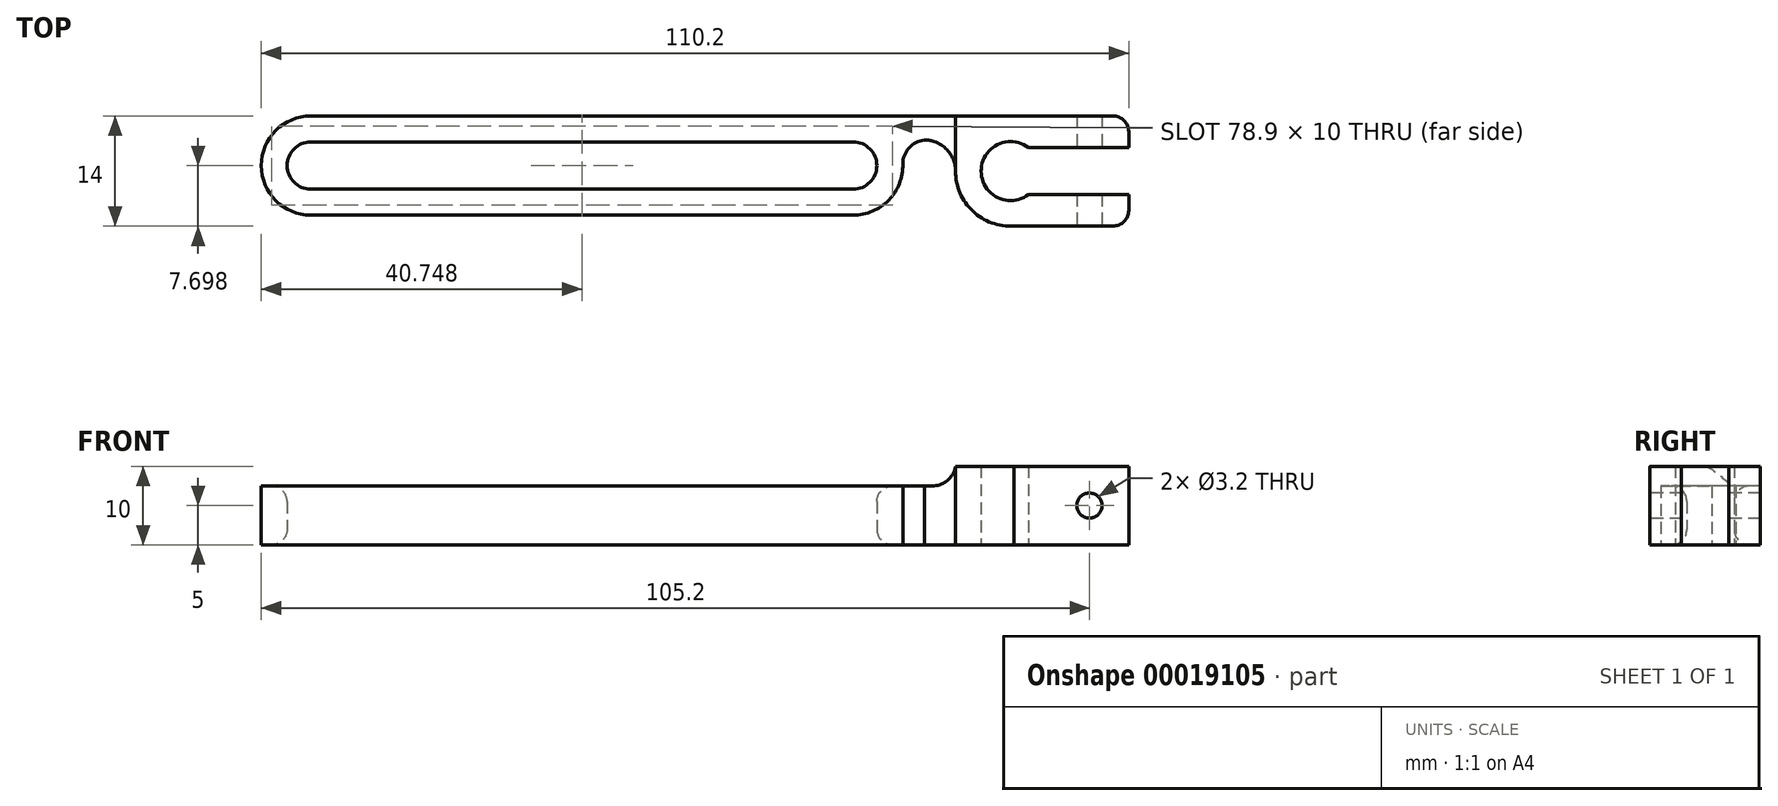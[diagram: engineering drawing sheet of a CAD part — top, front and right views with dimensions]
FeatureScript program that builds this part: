
annotation { "Feature Type Name" : "Feature", "Feature Type Description" : "" }
export const myFeature = defineFeature(function(context is Context, id is Id, definition is map)
    precondition{}
    {
        {
            var Q0;
            Q0=qCreatedBy(makeId("Top.planeOp"),FACE);
            var sketch = newSketch(context, id + "F0", { "sketchPlane" : qUnion([Q0])});
            skArc(sketch, "E0", {"start": v(-12.75, 8.6) * mm, "mid": v(-18.75, 5.59) * mm, "end": v(-12.73, 2.6) * mm});
            skArc(sketch, "E1", {"start": v(-22, 5.6) * mm, "mid": v(-19.8, 0.5) * mm, "end": v(-14.6, -1.4) * mm});
            skLineSegment(sketch, "E2.bottom", {"start": v(-15, 12.6) * mm, "end": v(-103.9, 12.6) * mm});
            skArc(sketch, "E3", {"start": v(-22, 5.6) * mm, "mid": v(-23.16, 8.4) * mm, "end": v(-25.95, 9.55) * mm});
            skLineSegment(sketch, "E4.bottom", {"start": v(-15, 12.6) * mm, "end": v(0, 12.6) * mm});
            skLineSegment(sketch, "E4.top", {"start": v(-15, -1.4) * mm, "end": v(0, -1.4) * mm});
            skLineSegment(sketch, "E4.right", {"start": v(0, 12.6) * mm, "end": v(0, 8.6) * mm});
            skLineSegment(sketch, "E5.bottom", {"start": v(-12.73, 2.6) * mm, "end": v(0, 2.6) * mm});
            skLineSegment(sketch, "E5.top", {"start": v(-12.75, 8.6) * mm, "end": v(0, 8.6) * mm});
            skLineSegment(sketch, "E6.trimOffspring", {"start": v(0, 2.6) * mm, "end": v(0, -1.4) * mm});
            skArc(sketch, "E7", {"start": v(-103.9, 9.3) * mm, "mid": v(-106.9, 6.3) * mm, "end": v(-103.9, 3.3) * mm});
            skArc(sketch, "E8", {"start": v(-35, 3.3) * mm, "mid": v(-32, 6.3) * mm, "end": v(-35, 9.3) * mm});
            skPoint(sketch, "E9", {"position": v(-110.95, 6.3) * mm});
            skLineSegment(sketch, "E10", {"start": v(-103.9, 3.3) * mm, "end": v(-35, 3.3) * mm});
            skLineSegment(sketch, "E11", {"start": v(-103.9, 9.3) * mm, "end": v(-35, 9.3) * mm});
            skArc(sketch, "E12", {"start": v(-35, 0) * mm, "mid": v(-30.49, 1.9) * mm, "end": v(-28.7, 6.47) * mm});
            skArc(sketch, "E13", {"start": v(-103.9, 12.6) * mm, "mid": v(-110.2, 6.3) * mm, "end": v(-103.9, 0) * mm});
            skPoint(sketch, "E14.orphan", {"position": v(-110.95, 0) * mm});
            skPoint(sketch, "E15.left.end.orphan", {"position": v(-110.95, 9.55) * mm});
            skPoint(sketch, "E16.orphan", {"position": v(-110.95, 12.6) * mm});
            skLineSegment(sketch, "E17", {"start": v(-103.9, 0) * mm, "end": v(-35, 0) * mm});
            skArc(sketch, "E18", {"start": v(-25.95, 9.55) * mm, "mid": v(-27.91, 8.53) * mm, "end": v(-28.7, 6.47) * mm});
            skSolve(sketch);
        }
        {
            var Q0;
            Q0 = qSketchRegion(id + "F0", true);
            extrude(context, id + "F1", {"entities" : qUnion([Q0]), "depth" : 10 * mm});
        }
        {
            var Q0;
            Q0=makeQuery(id+"F1.opExtrude","SWEPT_FACE",FACE,{"disambiguationData":[OSD([sQuery(id+"F0.wireOp",EDGE,"E4.top")])]});
            var sketch = newSketch(context, id + "F2", { "sketchPlane" : qUnion([Q0])});
            skCircle(sketch, "E19", {"center": v(-5, 5) * mm, "radius": 1.6 * mm});
            skLineSegment(sketch, "E20.bottom", {"start": v(-22, 17.5) * mm, "end": v(-116.99, 17.5) * mm});
            skLineSegment(sketch, "E20.top", {"start": v(-22, 7.5) * mm, "end": v(-116.99, 7.5) * mm});
            skLineSegment(sketch, "E20.left", {"start": v(-22, 17.5) * mm, "end": v(-22, 7.5) * mm});
            skLineSegment(sketch, "E20.right", {"start": v(-116.99, 17.5) * mm, "end": v(-116.99, 7.5) * mm});
            skPoint(sketch, "E21", {"position": v(0, 5) * mm});
            skSolve(sketch);
        }
        {
            var Q0;
            Q0=qSketchRegion(id+"F2",true);
            extrude(context, id + "F3", {"entities" : qUnion([Q0]), "operationType" : NewBodyOperationType.REMOVE, "endBound" : BoundingType.THROUGH_ALL, "oppositeDirection" : true, "depth" : 25 * mm});
        }
        {
            var Q0;
            Q0=makeQuery(id+"F1.opExtrude","SWEPT_EDGE",EDGE,{"disambiguationData":[OSD([sQuery(id+"F0.wireOp",EDGE,"E2.bottom"),sQuery(id+"F0.wireOp",EDGE,"E2.right")])]});
            var Q1;
            Q1=makeQuery(id+"F1.opExtrude","SWEPT_EDGE",EDGE,{"disambiguationData":[OSD([sQuery(id+"F0.wireOp",EDGE,"E4.top"),sQuery(id+"F0.wireOp",EDGE,"E6.trimOffspring")])]});
            var Q2;
            Q2=makeQuery(id+"F1.opExtrude","SWEPT_EDGE",EDGE,{"disambiguationData":[OSD([sQuery(id+"F0.wireOp",EDGE,"E4.bottom"),sQuery(id+"F0.wireOp",EDGE,"E4.right")])]});
            fillet(context, id + "F4", {"entities" : qUnion([Q0, Q1, Q2]), "radius" : 2 * mm, "tangentPropagation" : true, "allowEdgeOverflow" : false});
        }
        {
            var Q0;
            Q0 = qSketchRegion(id + "F2", true);
            extrude(context, id + "F5", {"entities" : qUnion([Q0]), "operationType" : NewBodyOperationType.REMOVE, "endBound" : BoundingType.THROUGH_ALL, "oppositeDirection" : true, "depth" : 25 * mm});
        }
        {
            var Q0;
            Q0=makeQuery(id+"F3.boolean.opBoolean","COPY",EDGE,{"derivedFrom":makeQuery(id+"F3.opExtrude","SWEPT_EDGE",EDGE,{"disambiguationData":[OSD([sQuery(id+"F2.wireOp",EDGE,"E20.top"),sQuery(id+"F2.wireOp",EDGE,"E20.left")])]})});
            fillet(context, id + "F6", {"entities" : qUnion([Q0]), "radius" : 3 * mm, "tangentPropagation" : true, "allowEdgeOverflow" : false});
        }
        {
            var Q0;
            Q0=makeQuery(id+"F3.boolean.opBoolean","INTERSECT",EDGE,{"derivedFrom":[makeQuery(id+"F1.opExtrude","SWEPT_FACE",FACE,{"disambiguationData":[OSD([sQuery(id+"F0.wireOp",EDGE,"E11")])]}),makeQuery(id+"F3.opExtrude","SWEPT_FACE",FACE,{"disambiguationData":[OSD([sQuery(id+"F2.wireOp",EDGE,"E20.top")])]})]});
            var Q1;
            Q1=makeQuery(id+"F3.boolean.opBoolean","INTERSECT",EDGE,{"derivedFrom":[makeQuery(id+"F1.opExtrude","SWEPT_FACE",FACE,{"disambiguationData":[OSD([sQuery(id+"F0.wireOp",EDGE,"E7")])]}),makeQuery(id+"F3.opExtrude","SWEPT_FACE",FACE,{"disambiguationData":[OSD([sQuery(id+"F2.wireOp",EDGE,"E20.top")])]})]});
            var Q2;
            Q2=makeQuery(id+"F3.boolean.opBoolean","INTERSECT",EDGE,{"derivedFrom":[makeQuery(id+"F1.opExtrude","SWEPT_FACE",FACE,{"disambiguationData":[OSD([sQuery(id+"F0.wireOp",EDGE,"E10")])]}),makeQuery(id+"F3.opExtrude","SWEPT_FACE",FACE,{"disambiguationData":[OSD([sQuery(id+"F2.wireOp",EDGE,"E20.top")])]})]});
            var Q3;
            Q3=makeQuery(id+"F3.boolean.opBoolean","INTERSECT",EDGE,{"derivedFrom":[makeQuery(id+"F1.opExtrude","SWEPT_FACE",FACE,{"disambiguationData":[OSD([sQuery(id+"F0.wireOp",EDGE,"E8")])]}),makeQuery(id+"F3.opExtrude","SWEPT_FACE",FACE,{"disambiguationData":[OSD([sQuery(id+"F2.wireOp",EDGE,"E20.top")])]})]});
            fillet(context, id + "F7", {"entities" : qUnion([Q0, Q1, Q2, Q3]), "radius" : 2 * mm, "tangentPropagation" : true, "allowEdgeOverflow" : false});
        }
        {
            var Q0;
            Q0=makeQuery(id+"F1.opExtrude","CAP_EDGE",EDGE,{"disambiguationData":[OSD([sQuery(id+"F0.wireOp",EDGE,"E11")])],"isStart":true});
            var Q1;
            Q1=makeQuery(id+"F1.opExtrude","CAP_EDGE",EDGE,{"disambiguationData":[OSD([sQuery(id+"F0.wireOp",EDGE,"E8")])],"isStart":true});
            var Q2;
            Q2=makeQuery(id+"F1.opExtrude","CAP_EDGE",EDGE,{"disambiguationData":[OSD([sQuery(id+"F0.wireOp",EDGE,"E10")])],"isStart":true});
            var Q3;
            Q3=makeQuery(id+"F1.opExtrude","CAP_EDGE",EDGE,{"disambiguationData":[OSD([sQuery(id+"F0.wireOp",EDGE,"E7")])],"isStart":true});
            fillet(context, id + "F8", {"entities" : qUnion([Q0, Q1, Q2, Q3]), "radius" : 2 * mm, "tangentPropagation" : true, "allowEdgeOverflow" : false});
        }
    });
